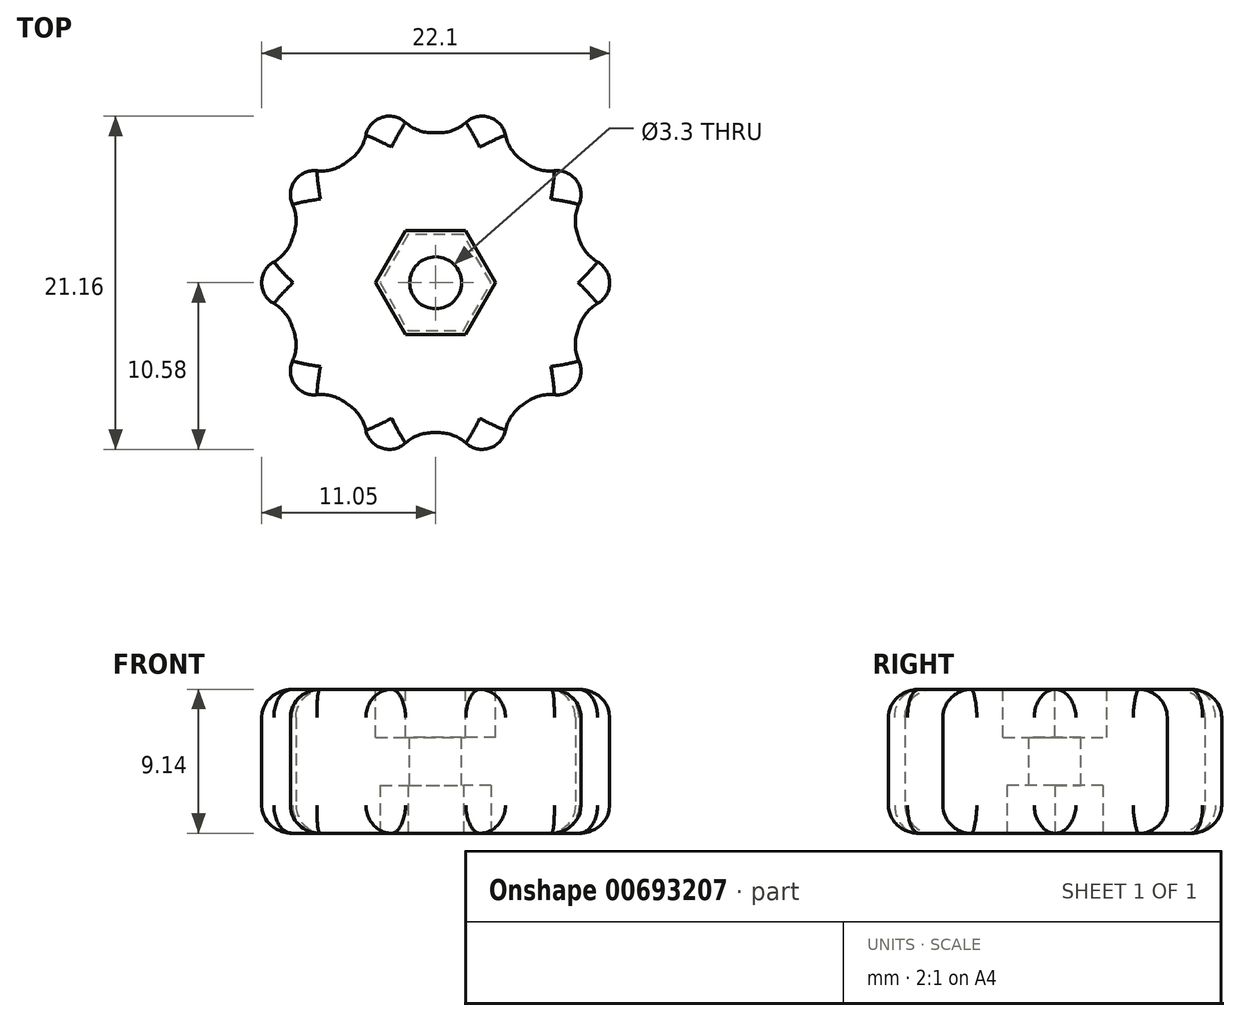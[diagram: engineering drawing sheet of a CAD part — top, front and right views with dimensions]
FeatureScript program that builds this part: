
annotation { "Feature Type Name" : "Feature", "Feature Type Description" : "" }
export const myFeature = defineFeature(function(context is Context, id is Id, definition is map)
    precondition{}
    {
        {
            var Q0;
            Q0=qCreatedBy(makeId("Top.planeOp"),FACE);
            var sketch = newSketch(context, id + "F0", { "sketchPlane" : qUnion([Q0])});
            skArc(sketch, "E0", {"start": v(-0.16, -9.52) * mm, "mid": v(0, -9.53) * mm, "end": v(0.16, -9.52) * mm});
            skArc(sketch, "E1", {"start": v(-10.28, 1.32) * mm, "mid": v(-11.05, 0) * mm, "end": v(-10.28, -1.32) * mm});
            skArc(sketch, "E2.1.0", {"start": v(-9.1, -4.97) * mm, "mid": v(-8.94, -6.5) * mm, "end": v(-7.54, -7.11) * mm});
            skArc(sketch, "E2.2.0", {"start": v(-4.44, -9.37) * mm, "mid": v(-3.41, -10.5) * mm, "end": v(-1.92, -10.19) * mm});
            skArc(sketch, "E2.3.0", {"start": v(1.92, -10.19) * mm, "mid": v(3.41, -10.5) * mm, "end": v(4.44, -9.37) * mm});
            skArc(sketch, "E2.4.0", {"start": v(7.54, -7.11) * mm, "mid": v(8.94, -6.5) * mm, "end": v(9.1, -4.97) * mm});
            skArc(sketch, "E2.5.0", {"start": v(10.28, -1.32) * mm, "mid": v(11.05, 0) * mm, "end": v(10.28, 1.32) * mm});
            skArc(sketch, "E2.6.0", {"start": v(9.1, 4.97) * mm, "mid": v(8.94, 6.5) * mm, "end": v(7.54, 7.11) * mm});
            skArc(sketch, "E2.7.0", {"start": v(4.44, 9.37) * mm, "mid": v(3.41, 10.5) * mm, "end": v(1.92, 10.19) * mm});
            skArc(sketch, "E2.8.0", {"start": v(-1.92, 10.19) * mm, "mid": v(-3.41, 10.5) * mm, "end": v(-4.44, 9.37) * mm});
            skArc(sketch, "E2.9.0", {"start": v(-7.54, 7.11) * mm, "mid": v(-8.94, 6.5) * mm, "end": v(-9.1, 4.97) * mm});
            skArc(sketch, "E3.trimOffspring", {"start": v(5.47, -7.8) * mm, "mid": v(5.6, -7.7) * mm, "end": v(5.73, -7.6) * mm});
            skArc(sketch, "E4.trimOffspring", {"start": v(9, -3.1) * mm, "mid": v(9.06, -2.94) * mm, "end": v(9.1, -2.79) * mm});
            skArc(sketch, "E5.trimOffspring", {"start": v(-5.73, -7.6) * mm, "mid": v(-5.6, -7.7) * mm, "end": v(-5.47, -7.8) * mm});
            skArc(sketch, "E6.trimOffspring", {"start": v(9.1, 2.79) * mm, "mid": v(9.06, 2.94) * mm, "end": v(9, 3.1) * mm});
            skArc(sketch, "E7.trimOffspring", {"start": v(5.73, 7.6) * mm, "mid": v(5.6, 7.7) * mm, "end": v(5.47, 7.8) * mm});
            skArc(sketch, "E8.trimOffspring", {"start": v(0.16, 9.52) * mm, "mid": v(0, 9.53) * mm, "end": v(-0.16, 9.52) * mm});
            skArc(sketch, "E9.trimOffspring", {"start": v(-9.1, -2.79) * mm, "mid": v(-9.06, -2.94) * mm, "end": v(-9, -3.1) * mm});
            skArc(sketch, "E10.trimOffspring", {"start": v(-9, 3.1) * mm, "mid": v(-9.06, 2.94) * mm, "end": v(-9.1, 2.79) * mm});
            skArc(sketch, "E11.trimOffspring", {"start": v(-5.47, 7.8) * mm, "mid": v(-5.6, 7.7) * mm, "end": v(-5.73, 7.6) * mm});
            skPoint(sketch, "E12.visualSharp", {"position": v(-9.4, -1.52) * mm});
            skArc(sketch, "E12.filletArc", {"start": v(-9.1, -2.79) * mm, "mid": v(-9.55, -1.94) * mm, "end": v(-10.28, -1.32) * mm});
            skPoint(sketch, "E13.visualSharp", {"position": v(-8.5, -4.3) * mm});
            skArc(sketch, "E13.filletArc", {"start": v(-9.1, -4.97) * mm, "mid": v(-8.87, -4.04) * mm, "end": v(-9, -3.1) * mm});
            skPoint(sketch, "E14.visualSharp", {"position": v(-9.4, 1.52) * mm});
            skArc(sketch, "E14.filletArc", {"start": v(-10.28, 1.32) * mm, "mid": v(-9.55, 1.94) * mm, "end": v(-9.1, 2.79) * mm});
            skPoint(sketch, "E15.visualSharp", {"position": v(-8.5, 4.3) * mm});
            skArc(sketch, "E15.filletArc", {"start": v(-9, 3.1) * mm, "mid": v(-8.87, 4.04) * mm, "end": v(-9.1, 4.97) * mm});
            skPoint(sketch, "E16.visualSharp", {"position": v(-6.71, 6.76) * mm});
            skArc(sketch, "E16.filletArc", {"start": v(-7.54, 7.11) * mm, "mid": v(-6.59, 7.19) * mm, "end": v(-5.73, 7.6) * mm});
            skPoint(sketch, "E17.visualSharp", {"position": v(-4.35, 8.47) * mm});
            skArc(sketch, "E17.filletArc", {"start": v(-5.47, 7.8) * mm, "mid": v(-4.8, 8.49) * mm, "end": v(-4.44, 9.37) * mm});
            skPoint(sketch, "E18.visualSharp", {"position": v(-6.71, -6.76) * mm});
            skArc(sketch, "E18.filletArc", {"start": v(-5.73, -7.6) * mm, "mid": v(-6.59, -7.19) * mm, "end": v(-7.54, -7.11) * mm});
            skPoint(sketch, "E19.visualSharp", {"position": v(-4.35, -8.47) * mm});
            skArc(sketch, "E19.filletArc", {"start": v(-4.44, -9.37) * mm, "mid": v(-4.8, -8.49) * mm, "end": v(-5.47, -7.8) * mm});
            skPoint(sketch, "E20.visualSharp", {"position": v(-1.46, -9.41) * mm});
            skArc(sketch, "E20.filletArc", {"start": v(-0.16, -9.52) * mm, "mid": v(-1.1, -9.69) * mm, "end": v(-1.92, -10.19) * mm});
            skPoint(sketch, "E21.visualSharp", {"position": v(1.46, -9.41) * mm});
            skArc(sketch, "E21.filletArc", {"start": v(1.92, -10.19) * mm, "mid": v(1.1, -9.69) * mm, "end": v(0.16, -9.52) * mm});
            skPoint(sketch, "E22.visualSharp", {"position": v(6.71, -6.76) * mm});
            skArc(sketch, "E22.filletArc", {"start": v(7.54, -7.11) * mm, "mid": v(6.59, -7.19) * mm, "end": v(5.73, -7.6) * mm});
            skPoint(sketch, "E23.visualSharp", {"position": v(4.35, -8.47) * mm});
            skArc(sketch, "E23.filletArc", {"start": v(5.47, -7.8) * mm, "mid": v(4.8, -8.49) * mm, "end": v(4.44, -9.37) * mm});
            skPoint(sketch, "E24.visualSharp", {"position": v(8.5, -4.3) * mm});
            skArc(sketch, "E24.filletArc", {"start": v(9, -3.1) * mm, "mid": v(8.87, -4.04) * mm, "end": v(9.1, -4.97) * mm});
            skPoint(sketch, "E25.visualSharp", {"position": v(9.4, 1.52) * mm});
            skArc(sketch, "E25.filletArc", {"start": v(9.1, 2.79) * mm, "mid": v(9.55, 1.94) * mm, "end": v(10.28, 1.32) * mm});
            skPoint(sketch, "E26.visualSharp", {"position": v(8.5, 4.3) * mm});
            skArc(sketch, "E26.filletArc", {"start": v(9.1, 4.97) * mm, "mid": v(8.87, 4.04) * mm, "end": v(9, 3.1) * mm});
            skPoint(sketch, "E27.visualSharp", {"position": v(6.71, 6.76) * mm});
            skArc(sketch, "E27.filletArc", {"start": v(5.73, 7.6) * mm, "mid": v(6.59, 7.19) * mm, "end": v(7.54, 7.11) * mm});
            skPoint(sketch, "E28.visualSharp", {"position": v(4.35, 8.47) * mm});
            skArc(sketch, "E28.filletArc", {"start": v(4.44, 9.37) * mm, "mid": v(4.8, 8.49) * mm, "end": v(5.47, 7.8) * mm});
            skPoint(sketch, "E29.visualSharp", {"position": v(1.46, 9.41) * mm});
            skArc(sketch, "E29.filletArc", {"start": v(0.16, 9.52) * mm, "mid": v(1.1, 9.69) * mm, "end": v(1.92, 10.19) * mm});
            skPoint(sketch, "E30.visualSharp", {"position": v(-1.46, 9.41) * mm});
            skArc(sketch, "E30.filletArc", {"start": v(-1.92, 10.19) * mm, "mid": v(-1.1, 9.69) * mm, "end": v(-0.16, 9.52) * mm});
            skPoint(sketch, "E31.visualSharp", {"position": v(9.4, -1.52) * mm});
            skArc(sketch, "E31.filletArc", {"start": v(10.28, -1.32) * mm, "mid": v(9.55, -1.94) * mm, "end": v(9.1, -2.79) * mm});
            skSolve(sketch);
        }
        {
            var Q0;
            Q0 = qSketchRegion(id + "F0", true);
            extrude(context, id + "F1", {"entities" : qUnion([Q0]), "depth" : 9.14 * mm, "offsetDistance" : 25.4 * mm});
        }
        {
            var Q0;
            Q0=makeQuery(id+"F1.opExtrude","CAP_EDGE",EDGE,{"disambiguationData":[OSD([sQuery(id+"F0.wireOp",EDGE,"E24.filletArc")])],"isStart":false});
            var Q1;
            Q1=makeQuery(id+"F1.opExtrude","CAP_EDGE",EDGE,{"disambiguationData":[OSD([sQuery(id+"F0.wireOp",EDGE,"E28.filletArc")])],"isStart":true});
            fillet(context, id + "F2", {"entities" : qUnion([Q0, Q1]), "radius" : 1.78 * mm, "tangentPropagation" : true, "allowEdgeOverflow" : false});
        }
        {
            var Q0;
            Q0=makeQuery(id+"F1.opExtrude","CAP_FACE",FACE,{"disambiguationData":[OSD([sQuery(id+"F0.wireOp",EDGE,"E0"),sQuery(id+"F0.wireOp",EDGE,"E1"),sQuery(id+"F0.wireOp",EDGE,"E2.1.0"),sQuery(id+"F0.wireOp",EDGE,"E2.2.0"),sQuery(id+"F0.wireOp",EDGE,"E2.3.0"),sQuery(id+"F0.wireOp",EDGE,"E2.4.0"),sQuery(id+"F0.wireOp",EDGE,"E2.5.0"),sQuery(id+"F0.wireOp",EDGE,"E2.6.0"),sQuery(id+"F0.wireOp",EDGE,"E2.7.0"),sQuery(id+"F0.wireOp",EDGE,"E2.8.0"),sQuery(id+"F0.wireOp",EDGE,"E2.9.0"),sQuery(id+"F0.wireOp",EDGE,"E3.trimOffspring"),sQuery(id+"F0.wireOp",EDGE,"E4.trimOffspring"),sQuery(id+"F0.wireOp",EDGE,"E5.trimOffspring"),sQuery(id+"F0.wireOp",EDGE,"E6.trimOffspring"),sQuery(id+"F0.wireOp",EDGE,"E7.trimOffspring"),sQuery(id+"F0.wireOp",EDGE,"E8.trimOffspring"),sQuery(id+"F0.wireOp",EDGE,"E9.trimOffspring"),sQuery(id+"F0.wireOp",EDGE,"E10.trimOffspring"),sQuery(id+"F0.wireOp",EDGE,"E11.trimOffspring"),sQuery(id+"F0.wireOp",EDGE,"E12.filletArc"),sQuery(id+"F0.wireOp",EDGE,"E13.filletArc"),sQuery(id+"F0.wireOp",EDGE,"E14.filletArc"),sQuery(id+"F0.wireOp",EDGE,"E15.filletArc"),sQuery(id+"F0.wireOp",EDGE,"E16.filletArc"),sQuery(id+"F0.wireOp",EDGE,"E17.filletArc"),sQuery(id+"F0.wireOp",EDGE,"E18.filletArc"),sQuery(id+"F0.wireOp",EDGE,"E19.filletArc"),sQuery(id+"F0.wireOp",EDGE,"E20.filletArc"),sQuery(id+"F0.wireOp",EDGE,"E21.filletArc"),sQuery(id+"F0.wireOp",EDGE,"E22.filletArc"),sQuery(id+"F0.wireOp",EDGE,"E23.filletArc"),sQuery(id+"F0.wireOp",EDGE,"E24.filletArc"),sQuery(id+"F0.wireOp",EDGE,"E25.filletArc"),sQuery(id+"F0.wireOp",EDGE,"E26.filletArc"),sQuery(id+"F0.wireOp",EDGE,"E27.filletArc"),sQuery(id+"F0.wireOp",EDGE,"E28.filletArc"),sQuery(id+"F0.wireOp",EDGE,"E29.filletArc"),sQuery(id+"F0.wireOp",EDGE,"E30.filletArc"),sQuery(id+"F0.wireOp",EDGE,"E31.filletArc")])],"isStart":false});
            var sketch = newSketch(context, id + "F3", { "sketchPlane" : qUnion([Q0])});
            skCircle(sketch, "E32.cCircle", {"center": v(0, 0) * mm, "radius": 3.3 * mm, "construction": true});
            skLineSegment(sketch, "E32.0", {"start": v(-1.9, 3.3) * mm, "end": v(1.9, 3.3) * mm});
            skLineSegment(sketch, "E32.1", {"start": v(1.9, 3.3) * mm, "end": v(3.81, 0) * mm});
            skLineSegment(sketch, "E32.2", {"start": v(3.81, 0) * mm, "end": v(1.9, -3.3) * mm});
            skLineSegment(sketch, "E32.3", {"start": v(1.9, -3.3) * mm, "end": v(-1.9, -3.3) * mm});
            skLineSegment(sketch, "E32.4", {"start": v(-1.9, -3.3) * mm, "end": v(-3.81, 0) * mm});
            skLineSegment(sketch, "E32.5", {"start": v(-3.81, 0) * mm, "end": v(-1.9, 3.3) * mm});
            skPoint(sketch, "E32.0.midPoint", {"position": v(0, 3.3) * mm});
            skSolve(sketch);
        }
        {
            var Q0;
            Q0 = qSketchRegion(id + "F3", true);
            var Q1;
            Q1=sQuery(id+"F3.wireOp",EDGE,"E32.4");
            var Q2;
            Q2=sQuery(id+"F3.wireOp",EDGE,"E32.3");
            extrude(context, id + "F4", {"entities" : qUnion([Q0]), "operationType" : NewBodyOperationType.REMOVE, "surfaceEntities" : qUnion([Q1, Q2]), "oppositeDirection" : true, "depth" : 3.05 * mm, "offsetDistance" : 25.4 * mm});
        }
        {
            var Q0;
            Q0=makeQuery(id+"F4.boolean.opBoolean","COPY",FACE,{"derivedFrom":makeQuery(id+"F4.opExtrude","CAP_FACE",FACE,{"disambiguationData":[OSD([sQuery(id+"F3.wireOp",EDGE,"E32.0"),sQuery(id+"F3.wireOp",EDGE,"E32.1"),sQuery(id+"F3.wireOp",EDGE,"E32.2"),sQuery(id+"F3.wireOp",EDGE,"E32.3"),sQuery(id+"F3.wireOp",EDGE,"E32.4"),sQuery(id+"F3.wireOp",EDGE,"E32.5")])],"isStart":false})});
            var sketch = newSketch(context, id + "F5", { "sketchPlane" : qUnion([Q0])});
            skCircle(sketch, "E33", {"center": v(0, 0) * mm, "radius": 0.96 * mm});
            skLineSegment(sketch, "E34", {"start": v(-0.96, 0) * mm, "end": v(0.96, 0) * mm});
            skLineSegment(sketch, "E35", {"start": v(0, 0.96) * mm, "end": v(0, -0.96) * mm});
            skSolve(sketch);
        }
        {
            var Q0;
            Q0=sQuery(id+"F5.wireOp",VERTEX,"E33.center");
            var Q1;
            Q1=makeQuery(id+"F1.opExtrude","SWEPT_BODY",BODY,{"disambiguationData":[OSD([sQuery(id+"F0.wireOp",EDGE,"E0"),sQuery(id+"F0.wireOp",EDGE,"E1"),sQuery(id+"F0.wireOp",EDGE,"E2.1.0"),sQuery(id+"F0.wireOp",EDGE,"E2.2.0"),sQuery(id+"F0.wireOp",EDGE,"E2.3.0"),sQuery(id+"F0.wireOp",EDGE,"E2.4.0"),sQuery(id+"F0.wireOp",EDGE,"E2.5.0"),sQuery(id+"F0.wireOp",EDGE,"E2.6.0"),sQuery(id+"F0.wireOp",EDGE,"E2.7.0"),sQuery(id+"F0.wireOp",EDGE,"E2.8.0"),sQuery(id+"F0.wireOp",EDGE,"E2.9.0"),sQuery(id+"F0.wireOp",EDGE,"E3.trimOffspring"),sQuery(id+"F0.wireOp",EDGE,"E4.trimOffspring"),sQuery(id+"F0.wireOp",EDGE,"E5.trimOffspring"),sQuery(id+"F0.wireOp",EDGE,"E6.trimOffspring"),sQuery(id+"F0.wireOp",EDGE,"E7.trimOffspring"),sQuery(id+"F0.wireOp",EDGE,"E8.trimOffspring"),sQuery(id+"F0.wireOp",EDGE,"E9.trimOffspring"),sQuery(id+"F0.wireOp",EDGE,"E10.trimOffspring"),sQuery(id+"F0.wireOp",EDGE,"E11.trimOffspring"),sQuery(id+"F0.wireOp",EDGE,"E12.filletArc"),sQuery(id+"F0.wireOp",EDGE,"E13.filletArc"),sQuery(id+"F0.wireOp",EDGE,"E14.filletArc"),sQuery(id+"F0.wireOp",EDGE,"E15.filletArc"),sQuery(id+"F0.wireOp",EDGE,"E16.filletArc"),sQuery(id+"F0.wireOp",EDGE,"E17.filletArc"),sQuery(id+"F0.wireOp",EDGE,"E18.filletArc"),sQuery(id+"F0.wireOp",EDGE,"E19.filletArc"),sQuery(id+"F0.wireOp",EDGE,"E20.filletArc"),sQuery(id+"F0.wireOp",EDGE,"E21.filletArc"),sQuery(id+"F0.wireOp",EDGE,"E22.filletArc"),sQuery(id+"F0.wireOp",EDGE,"E23.filletArc"),sQuery(id+"F0.wireOp",EDGE,"E24.filletArc"),sQuery(id+"F0.wireOp",EDGE,"E25.filletArc"),sQuery(id+"F0.wireOp",EDGE,"E26.filletArc"),sQuery(id+"F0.wireOp",EDGE,"E27.filletArc"),sQuery(id+"F0.wireOp",EDGE,"E28.filletArc"),sQuery(id+"F0.wireOp",EDGE,"E29.filletArc"),sQuery(id+"F0.wireOp",EDGE,"E30.filletArc"),sQuery(id+"F0.wireOp",EDGE,"E31.filletArc")])]});
            hole(context, id + "F6", {"style" : HoleStyle.SIMPLE, "endStyle" : HoleEndStyle.THROUGH, "standardTappedOrClearance" : lookupTablePath({ "standard" : "ISO", "fit" : "Normal", "size" : "M3", "type" : "Clearance" }), "standardBlindInLast" : lookupTablePath({ "fit" : "Standard", "standard" : "ISO", "size" : "M3", "type" : "Clearance" }), "holeDiameter" : 3.3 * mm, "majorDiameter" : 6.35 * mm, "isTappedThrough" : true, "tappedDepth" : 12.7 * mm, "tapClearance" : 3, "locations" : qUnion([Q0]), "scope" : qUnion([Q1])});
        }
        {
            var Q0;
            Q0=makeQuery(id+"F1.opExtrude","CAP_FACE",FACE,{"disambiguationData":[OSD([sQuery(id+"F0.wireOp",EDGE,"E0"),sQuery(id+"F0.wireOp",EDGE,"E1"),sQuery(id+"F0.wireOp",EDGE,"E2.1.0"),sQuery(id+"F0.wireOp",EDGE,"E2.2.0"),sQuery(id+"F0.wireOp",EDGE,"E2.3.0"),sQuery(id+"F0.wireOp",EDGE,"E2.4.0"),sQuery(id+"F0.wireOp",EDGE,"E2.5.0"),sQuery(id+"F0.wireOp",EDGE,"E2.6.0"),sQuery(id+"F0.wireOp",EDGE,"E2.7.0"),sQuery(id+"F0.wireOp",EDGE,"E2.8.0"),sQuery(id+"F0.wireOp",EDGE,"E2.9.0"),sQuery(id+"F0.wireOp",EDGE,"E3.trimOffspring"),sQuery(id+"F0.wireOp",EDGE,"E4.trimOffspring"),sQuery(id+"F0.wireOp",EDGE,"E5.trimOffspring"),sQuery(id+"F0.wireOp",EDGE,"E6.trimOffspring"),sQuery(id+"F0.wireOp",EDGE,"E7.trimOffspring"),sQuery(id+"F0.wireOp",EDGE,"E8.trimOffspring"),sQuery(id+"F0.wireOp",EDGE,"E9.trimOffspring"),sQuery(id+"F0.wireOp",EDGE,"E10.trimOffspring"),sQuery(id+"F0.wireOp",EDGE,"E11.trimOffspring"),sQuery(id+"F0.wireOp",EDGE,"E12.filletArc"),sQuery(id+"F0.wireOp",EDGE,"E13.filletArc"),sQuery(id+"F0.wireOp",EDGE,"E14.filletArc"),sQuery(id+"F0.wireOp",EDGE,"E15.filletArc"),sQuery(id+"F0.wireOp",EDGE,"E16.filletArc"),sQuery(id+"F0.wireOp",EDGE,"E17.filletArc"),sQuery(id+"F0.wireOp",EDGE,"E18.filletArc"),sQuery(id+"F0.wireOp",EDGE,"E19.filletArc"),sQuery(id+"F0.wireOp",EDGE,"E20.filletArc"),sQuery(id+"F0.wireOp",EDGE,"E21.filletArc"),sQuery(id+"F0.wireOp",EDGE,"E22.filletArc"),sQuery(id+"F0.wireOp",EDGE,"E23.filletArc"),sQuery(id+"F0.wireOp",EDGE,"E24.filletArc"),sQuery(id+"F0.wireOp",EDGE,"E25.filletArc"),sQuery(id+"F0.wireOp",EDGE,"E26.filletArc"),sQuery(id+"F0.wireOp",EDGE,"E27.filletArc"),sQuery(id+"F0.wireOp",EDGE,"E28.filletArc"),sQuery(id+"F0.wireOp",EDGE,"E29.filletArc"),sQuery(id+"F0.wireOp",EDGE,"E30.filletArc"),sQuery(id+"F0.wireOp",EDGE,"E31.filletArc")])],"isStart":true});
            var sketch = newSketch(context, id + "F7", { "sketchPlane" : qUnion([Q0])});
            skCircle(sketch, "E36.cCircle", {"center": v(0, 0) * mm, "radius": 3.05 * mm, "construction": true});
            skLineSegment(sketch, "E36.0", {"start": v(-1.76, 3.05) * mm, "end": v(1.76, 3.05) * mm});
            skLineSegment(sketch, "E36.1", {"start": v(1.76, 3.05) * mm, "end": v(3.52, 0) * mm});
            skLineSegment(sketch, "E36.2", {"start": v(3.52, 0) * mm, "end": v(1.76, -3.05) * mm});
            skLineSegment(sketch, "E36.3", {"start": v(1.76, -3.05) * mm, "end": v(-1.76, -3.05) * mm});
            skLineSegment(sketch, "E36.4", {"start": v(-1.76, -3.05) * mm, "end": v(-3.52, 0) * mm});
            skLineSegment(sketch, "E36.5", {"start": v(-3.52, 0) * mm, "end": v(-1.76, 3.05) * mm});
            skPoint(sketch, "E36.0.midPoint", {"position": v(0, 3.05) * mm});
            skSolve(sketch);
        }
        {
            var Q0;
            Q0 = qSketchRegion(id + "F7", true);
            extrude(context, id + "F8", {"entities" : qUnion([Q0]), "operationType" : NewBodyOperationType.REMOVE, "oppositeDirection" : true, "depth" : 3.05 * mm, "offsetDistance" : 25.4 * mm});
        }
    });
